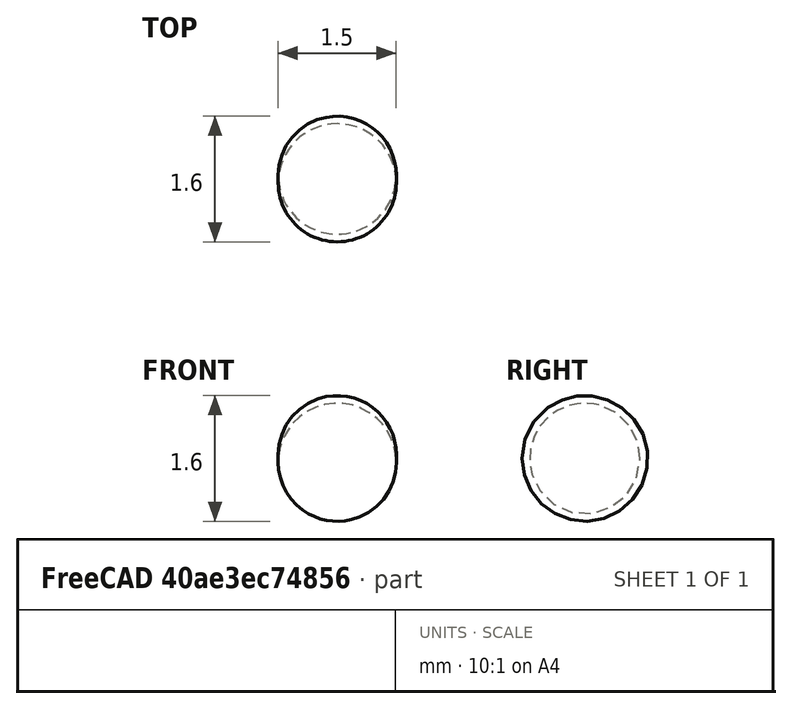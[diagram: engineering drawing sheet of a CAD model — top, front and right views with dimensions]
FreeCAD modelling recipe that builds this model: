
FCSTD DOCUMENT  (FreeCAD 1.1R41365 (Git))
Label: JointBall
License: All rights reserved
LicenseURL: https://en.wikipedia.org/wiki/All_rights_reserved
objects: App::Point×1, Sketcher::SketchObject×1, PartDesign::Revolution×1, PartDesign::Body×1
note: 6 computed .brp shape members not serialized (recipe doc carries the construction recipe); baked Part::Feature solids carry a one-line shape summary decoded from their .brp

FEATURE [App::Point] Origin001
  Role = Origin
FEATURE [Sketcher::SketchObject] Sketch
  ArcFitTolerance = 1e-06
  AttachmentSupport = -> [Origin]
  ExternalTypes = [0]
  FullyConstrained = false
  MakeInternals = false
  MapMode = 5
  sketch-geometry (2):
    g0: ArcOfCircle CenterX=0.0245252 CenterY=-0.048148 CenterZ=0 NormalX=0 NormalY=0 NormalZ=1 AngleXU=0 Radius=0.75 StartAngle=0.0642415 EndAngle=3.07735
    g1: LineSegment StartX=-0.723928 StartY=0 StartZ=0 EndX=0.772978 EndY=0 EndZ=0
  constraints (5):
    c: Coincident(g1,g0)
    c: Coincident(g1,g0)
    c: Horizontal(g1)
    c: Radius(g0) = 0.75
    c: PointOnObject(g0,g-1)
FEATURE [PartDesign::Revolution] Revolution
  Angle = 360
  Angle2 = 60
  Axis = (1,0,0)
  Base = (0,0,0)
  Profile = -> Sketch
  ReferenceAxis = -> Sketch [H_Axis]
  Refine = true
  Suppressed = false
  Type = 0
FEATURE [PartDesign::Body] Body  label="Ball"
  AllowCompound = false
  Group = -> [Sketch,Revolution]
  Origin = -> Origin
  Tip = -> Revolution
